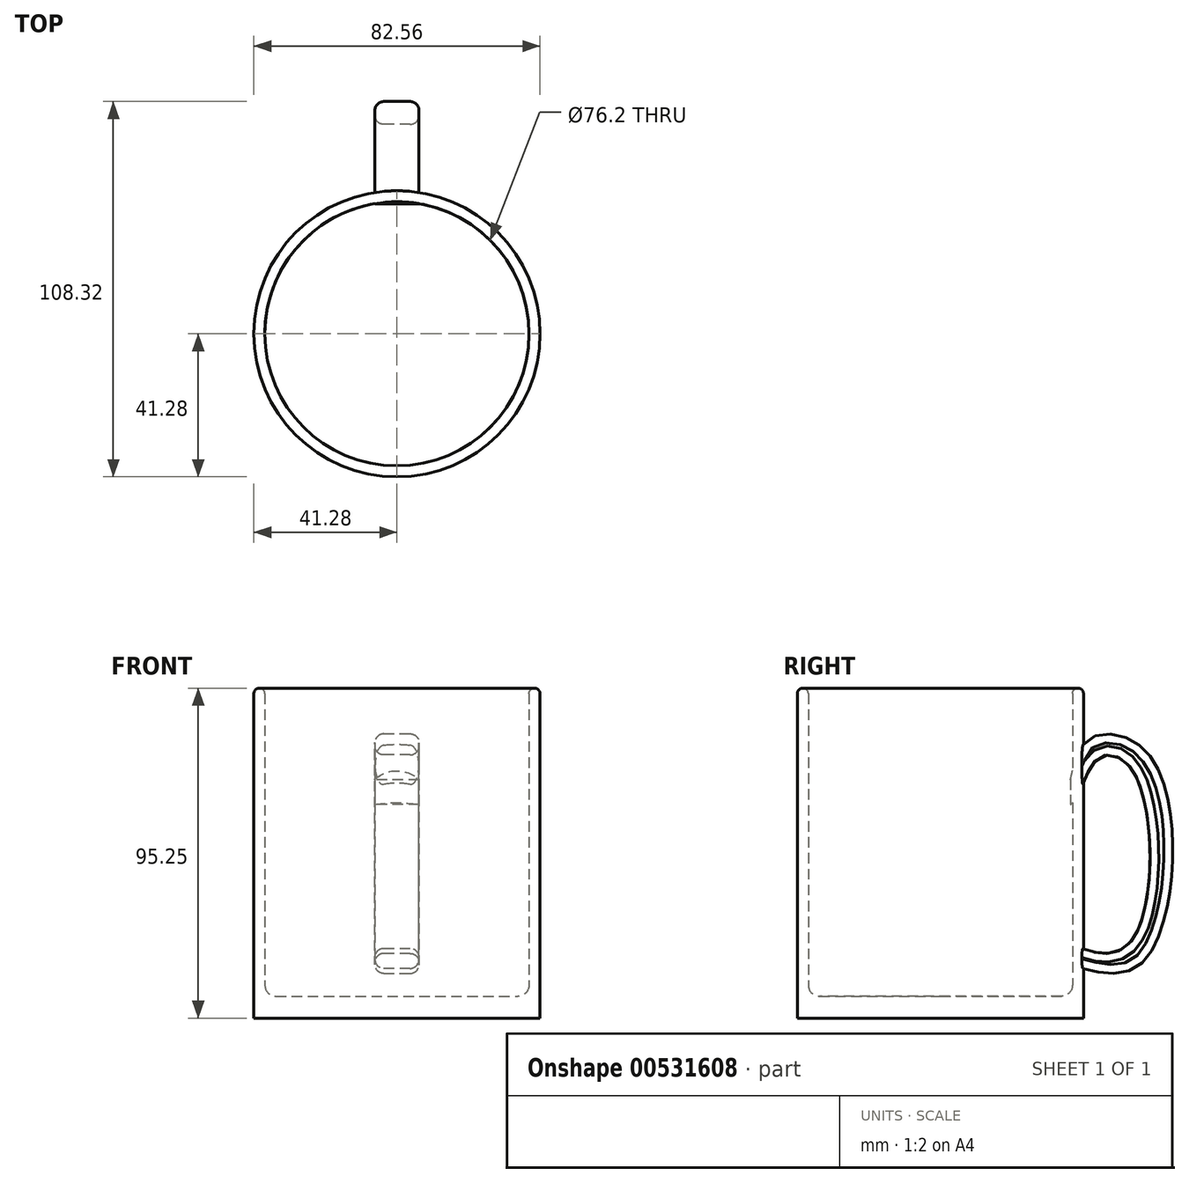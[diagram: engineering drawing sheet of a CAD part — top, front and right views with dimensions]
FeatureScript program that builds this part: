
annotation { "Feature Type Name" : "Feature", "Feature Type Description" : "" }
export const myFeature = defineFeature(function(context is Context, id is Id, definition is map)
    precondition{}
    {
        {
            var Q0;
            Q0=qCreatedBy(makeId("Right.planeOp"),FACE);
            var sketch = newSketch(context, id + "F0", { "sketchPlane" : qUnion([Q0])});
            skLineSegment(sketch, "E0.bottom", {"start": v(0, 0) * mm, "end": v(41.28, 0) * mm});
            skLineSegment(sketch, "E0.top", {"start": v(39.69, 95.25) * mm, "end": v(39.69, 95.25) * mm});
            skLineSegment(sketch, "E0.left", {"start": v(0, 0) * mm, "end": v(0, 6.35) * mm});
            skLineSegment(sketch, "E0.right", {"start": v(41.28, 0) * mm, "end": v(41.27, 93.66) * mm});
            skLineSegment(sketch, "E1", {"start": v(0, 6.35) * mm, "end": v(34.93, 6.35) * mm});
            skLineSegment(sketch, "E2", {"start": v(38.1, 9.52) * mm, "end": v(38.1, 93.66) * mm});
            skPoint(sketch, "E3.visualSharp", {"position": v(38.1, 6.35) * mm});
            skArc(sketch, "E3.filletArc", {"start": v(34.93, 6.35) * mm, "mid": v(37.17, 7.28) * mm, "end": v(38.1, 9.53) * mm});
            skPoint(sketch, "E4.visualSharp", {"position": v(38.1, 95.25) * mm});
            skArc(sketch, "E4.filletArc", {"start": v(39.69, 95.25) * mm, "mid": v(38.56, 94.79) * mm, "end": v(38.1, 93.66) * mm});
            skPoint(sketch, "E5.visualSharp", {"position": v(41.27, 95.25) * mm});
            skArc(sketch, "E5.filletArc", {"start": v(41.27, 93.66) * mm, "mid": v(40.81, 94.79) * mm, "end": v(39.69, 95.25) * mm});
            skSolve(sketch);
        }
        {
            var Q0;
            Q0=qCreatedBy(makeId("Right.planeOp"),FACE);
            var sketch = newSketch(context, id + "F1", { "sketchPlane" : qUnion([Q0])});
            skLineSegment(sketch, "E6", {"start": v(0, 0) * mm, "end": v(0, 69.17) * mm, "construction": true});
            skSolve(sketch);
        }
        {
            var Q0;
            Q0 = qSketchRegion(id + "F0", true);
            var Q1;
            Q1=sQuery(id+"F1.wireOp",EDGE,"E6");
            revolve(context, id + "F2", {"entities" : qUnion([Q0]), "axis" : qUnion([Q1]), "revolveType" : RevolveType.FULL});
        }
        {
            var Q0;
            Q0=qCreatedBy(makeId("Right.planeOp"),FACE);
            var sketch = newSketch(context, id + "F3", { "sketchPlane" : qUnion([Q0])});
            skFitSpline(sketch, "E7", {"points": [v(37.52, 68.84) * mm, v(43.58, 80.97) * mm, v(61.78, 73.76) * mm, v(59.12, 16.92) * mm, v(38.28, 15.1) * mm], "startDerivative": vector(18.16, 82.46) * mm, "endDerivative": vector(-102.79, 28.4) * mm});
            skFitSpline(sketch, "E8", {"points": [v(37.46, 61.61) * mm, v(40.67, 66.53) * mm, v(46.02, 75.3) * mm, v(55.85, 70.8) * mm, v(55.42, 22.7) * mm, v(38.53, 21.2) * mm], "startDerivative": vector(26.94, 18.25) * mm, "endDerivative": vector(-93.1, 45.65) * mm});
            skLineSegment(sketch, "E9", {"start": v(37.52, 68.84) * mm, "end": v(37.46, 61.61) * mm});
            skLineSegment(sketch, "E10", {"start": v(38.53, 21.2) * mm, "end": v(38.28, 15.1) * mm});
            skSolve(sketch);
        }
        {
            var Q0;
            Q0 = qSketchRegion(id + "F3", true);
            extrude(context, id + "F4", {"entities" : qUnion([Q0]), "operationType" : NewBodyOperationType.ADD, "depth" : 6.35 * mm, "offsetDistance" : 25.4 * mm, "hasSecondDirection" : true, "secondDirectionOppositeDirection" : true, "secondDirectionDepth" : 6.35 * mm});
        }
        {
            var Q0;
            {var subQ0=sQuery(id+"F3.wireOp",EDGE,"E7");Q0=makeQuery(id+"F4.boolean.opBoolean","SPLIT",EDGE,{"disambiguationData":[TD([makeQuery(id+"F2.opRevolve","SWEPT_FACE",FACE,{"disambiguationData":[OSD([sQuery(id+"F0.wireOp",EDGE,"E0.right")])]})])],"derivedFrom":makeQuery(id+"F4.opExtrude","CAP_EDGE",EDGE,{"disambiguationData":[OSD([subQ0])],"isStart":false})});}
            var Q1;
            {var subQ0=sQuery(id+"F3.wireOp",EDGE,"E7");Q1=makeQuery(id+"F4.boolean.opBoolean","SPLIT",EDGE,{"disambiguationData":[TD([makeQuery(id+"F2.opRevolve","SWEPT_FACE",FACE,{"disambiguationData":[OSD([sQuery(id+"F0.wireOp",EDGE,"E0.right")])]})])],"derivedFrom":makeQuery(id+"F4.opExtrude","CAP_EDGE",EDGE,{"disambiguationData":[OSD([subQ0])],"isStart":true})});}
            var Q2;
            {var subQ0=sQuery(id+"F3.wireOp",EDGE,"E8");Q2=makeQuery(id+"F4.boolean.opBoolean","SPLIT",EDGE,{"disambiguationData":[TD([makeQuery(id+"F2.opRevolve","SWEPT_FACE",FACE,{"disambiguationData":[OSD([sQuery(id+"F0.wireOp",EDGE,"E0.right")])]})])],"derivedFrom":makeQuery(id+"F4.opExtrude","CAP_EDGE",EDGE,{"disambiguationData":[OSD([subQ0])],"isStart":false})});}
            var Q3;
            {var subQ0=sQuery(id+"F3.wireOp",EDGE,"E8");Q3=makeQuery(id+"F4.boolean.opBoolean","SPLIT",EDGE,{"disambiguationData":[TD([makeQuery(id+"F2.opRevolve","SWEPT_FACE",FACE,{"disambiguationData":[OSD([sQuery(id+"F0.wireOp",EDGE,"E0.right")])]})])],"derivedFrom":makeQuery(id+"F4.opExtrude","CAP_EDGE",EDGE,{"disambiguationData":[OSD([subQ0])],"isStart":true})});}
            fillet(context, id + "F5", {"entities" : qUnion([Q0, Q1, Q2, Q3]), "radius" : 2.54 * mm, "tangentPropagation" : true, "allowEdgeOverflow" : false});
        }
    });
